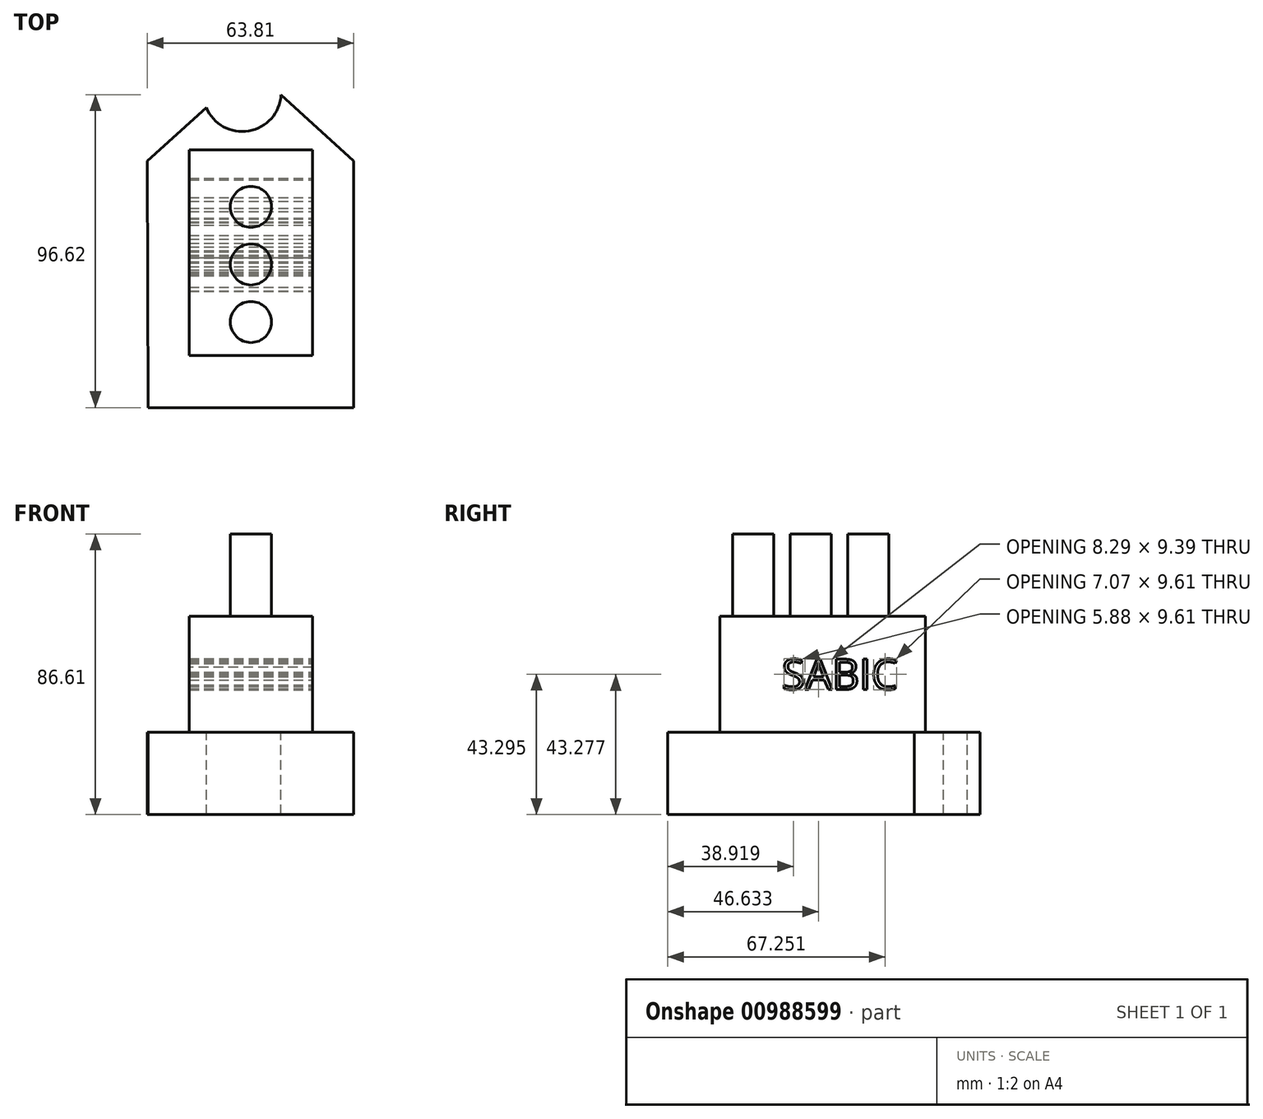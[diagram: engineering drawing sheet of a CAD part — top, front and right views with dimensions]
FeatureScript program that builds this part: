
annotation { "Feature Type Name" : "Feature", "Feature Type Description" : "" }
export const myFeature = defineFeature(function(context is Context, id is Id, definition is map)
    precondition{}
    {
        {
            var Q0;
            Q0=qCreatedBy(makeId("Top.planeOp"),FACE);
            var sketch = newSketch(context, id + "F0", { "sketchPlane" : qUnion([Q0])});
            skLineSegment(sketch, "E0", {"start": v(-31.75, -44.24) * mm, "end": v(31.75, -44.24) * mm});
            skLineSegment(sketch, "E1", {"start": v(31.75, -44.24) * mm, "end": v(31.75, 31.96) * mm});
            skLineSegment(sketch, "E2", {"start": v(31.75, 31.96) * mm, "end": v(0, 60.84) * mm});
            skLineSegment(sketch, "E3", {"start": v(0, 60.84) * mm, "end": v(-32.06, 31.95) * mm});
            skLineSegment(sketch, "E4", {"start": v(-32.06, 31.95) * mm, "end": v(-31.75, -44.24) * mm});
            skSolve(sketch);
        }
        {
            var Q0;
            Q0 = qSketchRegion(id + "F0", true);
            extrude(context, id + "F1", {"entities" : qUnion([Q0]), "depth" : 25.4 * mm, "offsetDistance" : 25.4 * mm});
        }
        {
            var Q0;
            Q0=makeQuery(id+"F1.opExtrude","CAP_FACE",FACE,{"disambiguationData":[OSD([sQuery(id+"F0.wireOp",EDGE,"E0"),sQuery(id+"F0.wireOp",EDGE,"E1"),sQuery(id+"F0.wireOp",EDGE,"E2"),sQuery(id+"F0.wireOp",EDGE,"E3"),sQuery(id+"F0.wireOp",EDGE,"E4")])],"isStart":false});
            var sketch = newSketch(context, id + "F2", { "sketchPlane" : qUnion([Q0])});
            skLineSegment(sketch, "E5.bottom", {"start": v(-19.05, 35.41) * mm, "end": v(19.05, 35.41) * mm});
            skLineSegment(sketch, "E5.top", {"start": v(-19.05, -28.09) * mm, "end": v(19.05, -28.09) * mm});
            skLineSegment(sketch, "E5.left", {"start": v(-19.05, 35.41) * mm, "end": v(-19.05, -28.09) * mm});
            skLineSegment(sketch, "E5.right", {"start": v(19.05, 35.41) * mm, "end": v(19.05, -28.09) * mm});
            skSolve(sketch);
        }
        {
            var Q0;
            Q0 = qSketchRegion(id + "F2", true);
            extrude(context, id + "F3", {"entities" : qUnion([Q0]), "operationType" : NewBodyOperationType.ADD, "depth" : 35.81 * mm, "offsetDistance" : 25.4 * mm});
        }
        {
            var Q0;
            Q0=makeQuery(id+"F3.opExtrude","CAP_FACE",FACE,{"disambiguationData":[OSD([sQuery(id+"F2.wireOp",EDGE,"E5.bottom"),sQuery(id+"F2.wireOp",EDGE,"E5.top"),sQuery(id+"F2.wireOp",EDGE,"E5.left"),sQuery(id+"F2.wireOp",EDGE,"E5.right")])],"isStart":false});
            var sketch = newSketch(context, id + "F4", { "sketchPlane" : qUnion([Q0])});
            skCircle(sketch, "E6", {"center": v(0, 17.78) * mm, "radius": 6.35 * mm});
            skCircle(sketch, "E7", {"center": v(0, 0) * mm, "radius": 6.35 * mm});
            skCircle(sketch, "E8", {"center": v(0, -17.78) * mm, "radius": 6.35 * mm});
            skSolve(sketch);
        }
        {
            var Q0;
            Q0 = qSketchRegion(id + "F4", true);
            extrude(context, id + "F5", {"entities" : qUnion([Q0]), "operationType" : NewBodyOperationType.ADD, "depth" : 25.4 * mm, "offsetDistance" : 25.4 * mm});
        }
        {
            var Q0;
            Q0=makeQuery(id+"F3.opExtrude","SWEPT_FACE",FACE,{"disambiguationData":[OSD([sQuery(id+"F2.wireOp",EDGE,"E5.right")])]});
            var sketch = newSketch(context, id + "F6", { "sketchPlane" : qUnion([Q0])});
            skText(sketch, "E9", { "text": "SABIC", "fontName": "OpenSans-Regular.ttf"});
            const initialGuessF6  = {"E9": [-0.00894, 0.0386, 1, 0, 0.00943]};
            skSetInitialGuess(sketch, initialGuessF6);
            skSolve(sketch);
        }
        {
            var Q0;
            Q0 = qSketchRegion(id + "F6", true);
            extrude(context, id + "F7", {"entities" : qUnion([Q0]), "operationType" : NewBodyOperationType.REMOVE, "oppositeDirection" : true, "depth" : 47.5 * mm, "offsetDistance" : 25.4 * mm});
        }
        {
            var Q0;
            Q0=makeQuery(id+"F1.opExtrude","CAP_FACE",FACE,{"disambiguationData":[OSD([sQuery(id+"F0.wireOp",EDGE,"E0"),sQuery(id+"F0.wireOp",EDGE,"E1"),sQuery(id+"F0.wireOp",EDGE,"E2"),sQuery(id+"F0.wireOp",EDGE,"E3"),sQuery(id+"F0.wireOp",EDGE,"E4")])],"isStart":false});
            var sketch = newSketch(context, id + "F8", { "sketchPlane" : qUnion([Q0])});
            skCircle(sketch, "E10", {"center": v(-2.68, 53.02) * mm, "radius": 12 * mm});
            skSolve(sketch);
        }
        {
            var Q0;
            Q0 = qSketchRegion(id + "F8", true);
            extrude(context, id + "F9", {"entities" : qUnion([Q0]), "operationType" : NewBodyOperationType.REMOVE, "oppositeDirection" : true, "depth" : 25.4 * mm, "offsetDistance" : 25.4 * mm});
        }
    });
